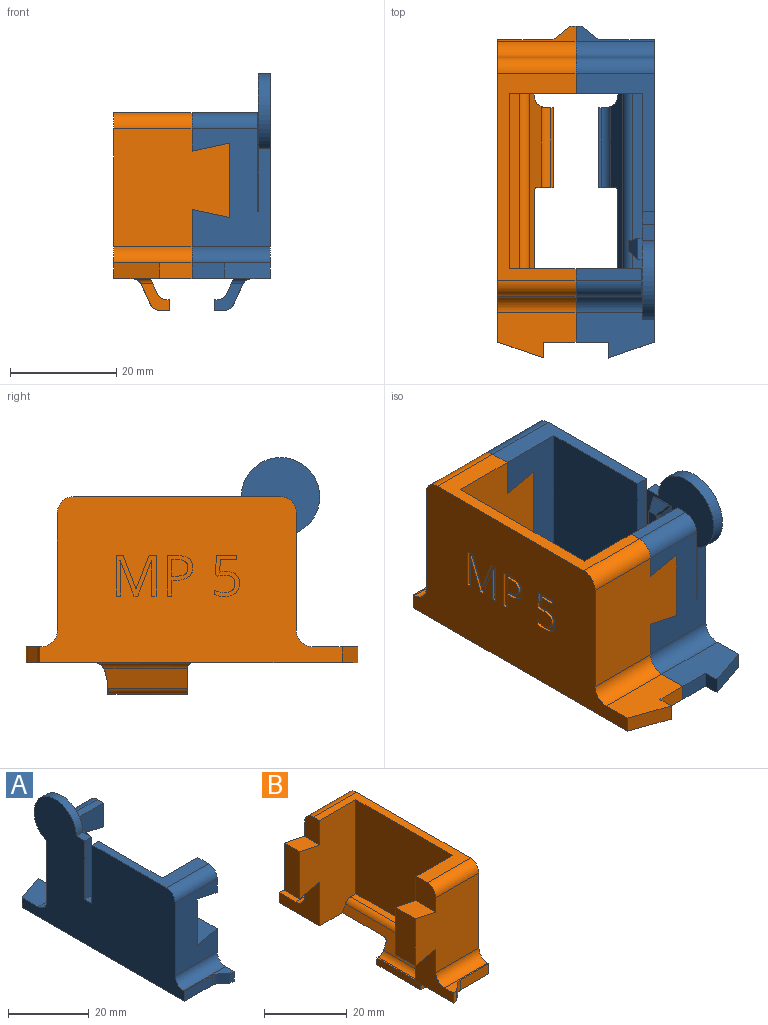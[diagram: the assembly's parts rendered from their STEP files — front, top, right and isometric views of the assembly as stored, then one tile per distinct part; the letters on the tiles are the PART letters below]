
ASSEMBLY  parts=2 mates=1
PART A: 65 faces, bbox 14.9x62.7x44.8 mm
  f0: plane 12.25x2.18mm, normal (0,0,1), area 26.6mm2, adj f1,f2,f4,f54
  f1: plane 31.2x12.45mm, normal (0,-1,0), area 284.9mm2, adj f0,f4,f8,f18,f28,f31,f34,f39
  f2: cylinder r=3mm len=12.25mm, axis (1,0,0), area 57.7mm2, adj f0,f4,f14,f54
  f3: plane 26.1x14.75mm, normal (0,0,1), area 107.6mm2, adj f6,f7,f17,f20,f31,f48
  f4: plane 7.2x5.18mm, normal (1,0,0), area 35.3mm2, adj f0,f1,f2,f14,f42
  f5: plane 22.2x14.75mm, normal (0,-1,0), area 239.9mm2, adj f7,f16,f17,f20,f38,f43,f44,f45
  f6: plane 31.2x12.45mm, normal (0,1,0), area 288.6mm2, adj f3,f7,f8,f18,f28,f31,f34,f38
  f7: plane 7.2x6.82mm, normal (1,0,0), area 47.2mm2, adj f3,f5,f6,f17,f43
  f8: plane 62.5x14.75mm, normal (0,0,-1), area 536.5mm2, adj f1,f6,f11,f12,f20,f21,f22,f23
  f9: plane 3x2.3mm, normal (0,0,1), area 6.9mm2, adj f20,f31,f46,f49
  f10: plane 14.75x8.6mm, normal (0,0,1), area 95.6mm2, adj f12,f15,f20,f23,f24,f39
  f11: cylinder r=4.2mm len=3mm, axis (0,0,-1), area 4.4mm2, adj f8,f13,f22,f38
  f12: plane 6.1x3mm, normal (0,1,0), area 18.3mm2, adj f8,f10,f23,f39
  f13: plane 14.75x2.9mm, normal (0,0,1), area 11.5mm2, adj f11,f16,f20,f21,f22,f37,f38
  f14: plane 22.2x14.75mm, normal (0,1,0), area 228.2mm2, adj f2,f4,f15,f20,f31,f39,f40,f41
  f15: cylinder r=3mm len=14.75mm, axis (1,0,0), area 69.5mm2, adj f10,f14,f20,f39
  f16: cylinder r=3mm len=14.75mm, axis (-1,0,0), area 69.5mm2, adj f5,f13,f20,f38
  f17: cylinder r=3mm len=14.75mm, axis (-1,0,0), area 69.5mm2, adj f3,f5,f7,f20
  f18: plane 33x1.8mm, normal (0,0,1), area 59.2mm2, adj f1,f6,f31,f34
  f19: plane 14.98x1.7mm, normal (0,0,-1), area 25.5mm2, adj f26,f29,f30,f36
  f20: plane 56.9x38.6mm, normal (-1,0,0), area 1504.8mm2, adj f3,f5,f8,f9,f10,f13,f14,f15
  f21: plane 9.74x3mm, normal (0,-1,0), area 29.2mm2, adj f8,f13,f20,f37
  f22: plane 3x2.32mm, normal (-0.63,-0.77,0), area 9mm2, adj f8,f11,f13,f37
  f23: plane 3x3mm, normal (1,0,0), area 9mm2, adj f8,f10,f12,f24
  f24: plane 8.65x3mm, normal (-0.33,0.94,0), area 27.5mm2, adj f8,f10,f20,f23
  f25: plane 15.86x3.81mm, normal (-0.91,0,-0.42), area 61.8mm2, adj f29,f30,f32,f36
  f26: plane 15.06x2.01mm, normal (1,0,0), area 30mm2, adj f19,f27,f29,f30
  f27: plane 15.04x0.42mm, normal (0,0,1), area 6.3mm2, adj f26,f29,f30,f35
  f28: plane 33.19x5.18mm, normal (0.91,0,0.42), area 127.4mm2, adj f1,f6,f8,f29,f30,f33,f34,f35
  f29: plane 5.3x5mm, normal (0,1,0), area 13.5mm2, adj f19,f25,f26,f27,f28,f32,f33,f35
  f30: extruded ~7.03x6mm, area 18.6mm2, adj f8,f19,f25,f26,f27,f28,f32,f35
  f31: plane 42.58x35.3mm, normal (1,0,0), area 1059.9mm2, adj f1,f3,f6,f9,f14,f18,f46,f47
  f32: cylinder r=2mm len=18.3mm, axis (0,-1,0), area 38.4mm2, adj f8,f25,f29,f30,f33
  f33: cylinder r=1mm len=3.94mm, axis (1,0,0), area 4.5mm2, adj f8,f28,f29,f32
  f34: cylinder r=2mm len=33mm, axis (0,1,0), area 75.1mm2, adj f1,f6,f18,f28
  f35: cylinder r=2mm len=15.24mm, axis (0,-1,0), area 34.4mm2, adj f27,f28,f29,f30
  f36: cylinder r=2mm len=14.98mm, axis (0,1,0), area 34.1mm2, adj f19,f25,f29,f30
  f37: cylinder r=2mm len=3mm, axis (0,0,-1), area 4.1mm2, adj f8,f13,f21,f22
  f38: plane 13x12.72mm, normal (1,0,0), area 108.4mm2, adj f5,f6,f8,f11,f13,f16,f44
  f39: plane 13.78x13mm, normal (1,0,0), area 95mm2, adj f1,f8,f10,f12,f14,f15,f41
  f40: plane 14x5.18mm, normal (1,0,0), area 72.5mm2, adj f1,f14,f41,f42
  f41: plane 7x5.18mm, normal (-0.21,0,0.98), area 37.1mm2, adj f1,f14,f39,f40
  f42: plane 7x5.18mm, normal (-0.21,0,-0.98), area 37.1mm2, adj f1,f4,f14,f40
  f43: plane 7x6.82mm, normal (-0.21,0,-0.98), area 48.9mm2, adj f5,f6,f7,f45
  f44: plane 7x6.82mm, normal (-0.21,0,0.98), area 48.9mm2, adj f5,f6,f38,f45
  f45: plane 14x6.82mm, normal (1,0,0), area 95.5mm2, adj f5,f6,f43,f44
  f46: plane 17.7x2.3mm, normal (0,-1,0), area 40.7mm2, adj f9,f20,f31,f47
  f47: plane 2.5x2.3mm, normal (0,0,1), area 5.8mm2, adj f20,f31,f46,f48
  f48: plane 17.7x2.3mm, normal (0,1,0), area 40.7mm2, adj f3,f20,f31,f47
  f49: cylinder r=7.4mm len=14.8mm, axis (-1,0,0), area 73.1mm2, adj f9,f14,f20,f31
  f50: plane 5.01x1.5mm, normal (0.32,-0.95,0), area 6.3mm2, adj f31,f51,f57,f59
  f51: plane 4x1.5mm, normal (-0.01,0,-1), area 4.5mm2, adj f31,f50,f52,f60
  f52: plane 5.01x1.5mm, normal (0.71,0.71,0), area 8.5mm2, adj f31,f51,f55,f61
  f53: plane 5.18x0.2mm, normal (0,0,1), area 1mm2, adj f1,f14,f31,f54
  f54: plane 18.55x5.18mm, normal (-1,0,0), area 94mm2, adj f0,f1,f2,f14,f53
  f55: plane 2.61x2.5mm, normal (0.31,0.86,-0.41), area 3.1mm2, adj f52,f56,f62,f64
  f56: plane 4x0.8mm, normal (-0.6,0,0.8), area 4mm2, adj f31,f55,f57,f64
  f57: plane 2.61x2.5mm, normal (0.12,-0.98,-0.16), area 2.7mm2, adj f50,f56,f58,f64
  f58: plane 1x0.33mm, normal (-0.31,0,0.95), area 0mm2, adj f57,f59,f63
  f59: plane 3.33x1mm, normal (0,-1,0), area 3.2mm2, adj f50,f58,f60,f63
  f60: plane 2x1mm, normal (0,0,-1), area 2mm2, adj f51,f59,f61,f63
  f61: plane 3.33x1mm, normal (0,1,0), area 3.2mm2, adj f52,f60,f62,f63
  f62: plane 1x0.33mm, normal (-0.31,0,0.95), area 0.1mm2, adj f55,f61,f63
  f63: plane 3.33x2mm, normal (1,0,0), area 6.7mm2, adj f58,f59,f60,f61,f62,f64
  f64: plane 4x2.28mm, normal (0.8,0,0.6), area 8.1mm2, adj f55,f56,f57,f63
PART B: 100 faces, bbox 21.9x62.7x37.4 mm
  f0: plane 56.9x31.2mm, normal (1,0,0), area 1378.8mm2, adj f3,f4,f5,f8,f9,f12,f13,f14
  f1: plane 13.78x13mm, normal (-1,0,0), area 95mm2, adj f3,f5,f11,f13,f22,f26,f43
  f2: plane 7.2x6.82mm, normal (-1,0,0), area 47.2mm2, adj f4,f14,f21,f29,f38
  f3: plane 62.5x14.75mm, normal (0,0,-1), area 536.5mm2, adj f0,f1,f6,f7,f8,f9,f10,f11
  f4: plane 39x14.75mm, normal (0,0,1), area 164.4mm2, adj f0,f2,f21,f22,f24,f28,f29,f37
  f5: plane 14.75x8.6mm, normal (0,0,1), area 95.6mm2, adj f0,f1,f9,f10,f11,f26
  f6: cylinder r=4.2mm len=3mm, axis (0,0,-1), area 4.4mm2, adj f3,f7,f12,f36
  f7: plane 3x2.32mm, normal (0.63,-0.77,0), area 9mm2, adj f3,f6,f12,f35
  f8: plane 9.74x3mm, normal (0,-1,0), area 29.2mm2, adj f0,f3,f12,f35
  f9: plane 8.65x3mm, normal (0.33,0.94,0), area 27.5mm2, adj f0,f3,f5,f10
  f10: plane 3x3mm, normal (-1,0,0), area 9mm2, adj f3,f5,f9,f11
  f11: plane 6.1x3mm, normal (0,1,0), area 18.3mm2, adj f1,f3,f5,f10
  f12: plane 14.75x2.9mm, normal (0,0,1), area 11.5mm2, adj f0,f6,f7,f8,f27,f35,f36
  f13: plane 22.2x21.75mm, normal (0,1,0), area 415mm2, adj f0,f1,f26,f28,f37,f41,f42,f43
  f14: plane 22.2x21.75mm, normal (0,-1,0), area 415mm2, adj f0,f2,f27,f29,f36,f38,f39,f40
  f15: plane 15.06x2.01mm, normal (-1,0,0), area 30mm2, adj f16,f19,f20,f23
  f16: plane 14.98x1.7mm, normal (0,0,-1), area 25.5mm2, adj f15,f20,f23,f34
  f17: plane 15.86x3.81mm, normal (0.91,0,-0.42), area 61.8mm2, adj f20,f23,f30,f34
  f18: plane 33.19x5.18mm, normal (-0.91,0,0.42), area 127.4mm2, adj f3,f20,f21,f22,f23,f31,f32,f33
  f19: plane 15.04x0.42mm, normal (0,0,1), area 6.3mm2, adj f15,f20,f23,f33
  f20: plane 5.3x5mm, normal (0,1,0), area 13.5mm2, adj f15,f16,f17,f18,f19,f30,f31,f33
  f21: plane 31.2x19.45mm, normal (0,1,0), area 463.6mm2, adj f2,f3,f4,f18,f24,f25,f32,f36
  f22: plane 31.2x19.45mm, normal (0,-1,0), area 463.6mm2, adj f1,f3,f4,f18,f24,f25,f32,f37
  f23: extruded ~7.03x6mm, area 18.6mm2, adj f3,f15,f16,f17,f18,f19,f30,f33
  f24: plane 33x27.9mm, normal (-1,0,0), area 920.7mm2, adj f4,f21,f22,f25
  f25: plane 33x1.8mm, normal (0,0,1), area 59.2mm2, adj f21,f22,f24,f32
  f26: cylinder r=3mm len=14.75mm, axis (1,0,0), area 69.5mm2, adj f0,f1,f5,f13
  f27: cylinder r=3mm len=14.75mm, axis (-1,0,0), area 69.5mm2, adj f0,f12,f14,f36
  f28: cylinder r=3mm len=14.75mm, axis (1,0,0), area 69.5mm2, adj f0,f4,f13,f37
  f29: cylinder r=3mm len=14.75mm, axis (-1,0,0), area 69.5mm2, adj f0,f2,f4,f14
  f30: cylinder r=2mm len=18.3mm, axis (0,1,0), area 38.4mm2, adj f3,f17,f20,f23,f31
  f31: cylinder r=1mm len=3.94mm, axis (-1,0,0), area 4.5mm2, adj f3,f18,f20,f30
  f32: cylinder r=2mm len=33mm, axis (0,-1,0), area 75.1mm2, adj f18,f21,f22,f25
  f33: cylinder r=2mm len=15.24mm, axis (0,-1,0), area 34.4mm2, adj f18,f19,f20,f23
  f34: cylinder r=2mm len=14.98mm, axis (0,1,0), area 34.1mm2, adj f16,f17,f20,f23
  f35: cylinder r=2mm len=3mm, axis (0,0,1), area 4.1mm2, adj f3,f7,f8,f12
  f36: plane 13x12.72mm, normal (-1,0,0), area 108.4mm2, adj f3,f6,f12,f14,f21,f27,f39
  f37: plane 7.2x5.18mm, normal (-1,0,0), area 35.3mm2, adj f4,f13,f22,f28,f41
  f38: plane 7x6.82mm, normal (0.21,0,0.98), area 48.9mm2, adj f2,f14,f21,f40
  f39: plane 7x6.82mm, normal (0.21,0,-0.98), area 48.9mm2, adj f14,f21,f36,f40
  f40: plane 14x6.82mm, normal (-1,0,0), area 95.5mm2, adj f14,f21,f38,f39
  f41: plane 7x5.18mm, normal (0.21,0,0.98), area 37.1mm2, adj f13,f22,f37,f42
  f42: plane 14x5.18mm, normal (-1,0,0), area 72.5mm2, adj f13,f22,f41,f43
  f43: plane 7x5.18mm, normal (0.21,0,-0.98), area 37.1mm2, adj f1,f13,f22,f42
  f44: plane 0.8x0.5mm, normal (0,0,-1), area 0.4mm2, adj f45,f58,f59,f99
  f45: plane 3.09x0.5mm, normal (0,-1,0), area 1.5mm2, adj f44,f46,f59,f99
  f46: plane 0.99x0.5mm, normal (0,0,1), area 0.5mm2, adj f45,f47,f59,f99
  f47: extruded ~1.54x0.5mm, area 0.8mm2, adj f46,f48,f59,f99
  f48: extruded ~1.12x0.5mm, area 0.6mm2, adj f47,f49,f59,f99
  f49: extruded ~1.22x0.53mm, area 0.7mm2, adj f48,f58,f59,f99
  f50: extruded ~1.78x0.79mm, area 1mm2, adj f0,f51,f57,f59
  f51: extruded ~2.85x2.22mm, area 2.1mm2, adj f0,f50,f52,f59
  f52: plane 1.98x0.5mm, normal (0,0,-1), area 1mm2, adj f0,f51,f53,f59
  f53: plane 7.62x0.5mm, normal (0,1,0), area 3.8mm2, adj f0,f52,f54,f59
  f54: plane 0.89x0.5mm, normal (0,0,1), area 0.4mm2, adj f0,f53,f55,f59
  f55: plane 3x0.5mm, normal (0,-1,0), area 1.5mm2, adj f0,f54,f56,f59
  f56: plane 0.9x0.5mm, normal (0,0,1), area 0.4mm2, adj f0,f55,f57,f59
  f57: extruded ~2.26x0.62mm, area 1.2mm2, adj f0,f50,f56,f59
  f58: extruded ~1.7x0.5mm, area 0.9mm2, adj f44,f49,f59,f99
  f59: plane 7.62x4.83mm, normal (1,0,0), area 14.3mm2, adj f44,f45,f46,f47,f48,f49,f50,f51
  f60: extruded ~1.89x0.6mm, area 1mm2, adj f0,f61,f78,f79
  f61: extruded ~1.19x0.5mm, area 0.6mm2, adj f0,f60,f62,f79
  f62: plane 2.29x0.5mm, normal (0,-1,0.08), area 1.1mm2, adj f0,f61,f63,f79
  f63: plane 3.05x0.5mm, normal (0,0,1), area 1.5mm2, adj f0,f62,f64,f79
  f64: plane 0.8x0.5mm, normal (0,-1,0), area 0.4mm2, adj f0,f63,f65,f79
  f65: plane 3.79x0.5mm, normal (0,0,-1), area 1.9mm2, adj f0,f64,f66,f79
  f66: plane 3.56x0.5mm, normal (0,1,-0.08), area 1.8mm2, adj f0,f65,f67,f79
  f67: plane 0.5x0.45mm, normal (0,0.54,0.84), area 0.3mm2, adj f0,f66,f68,f79
  f68: extruded ~1.32x0.5mm, area 0.7mm2, adj f0,f67,f69,f79
  f69: extruded ~1.95x1.59mm, area 1.4mm2, adj f0,f68,f70,f79
  f70: extruded ~1.25x0.51mm, area 0.7mm2, adj f0,f69,f71,f79
  f71: extruded ~1.42x0.5mm, area 0.8mm2, adj f0,f70,f72,f79
  f72: extruded ~1.07x0.5mm, area 0.5mm2, adj f0,f71,f73,f79
  f73: extruded ~0.91x0.5mm, area 0.5mm2, adj f0,f72,f74,f79
  f74: plane 0.83x0.5mm, normal (0,1,0), area 0.4mm2, adj f0,f73,f75,f79
  f75: extruded ~1.96x0.5mm, area 1mm2, adj f0,f74,f76,f79
  f76: extruded ~2.08x0.67mm, area 1.1mm2, adj f0,f75,f77,f79
  f77: extruded ~1.85x0.75mm, area 1mm2, adj f0,f76,f78,f79
  f78: extruded ~1.63x0.69mm, area 0.9mm2, adj f0,f60,f77,f79
  f79: plane 7.72x4.79mm, normal (1,0,0), area 13.5mm2, adj f60,f61,f62,f63,f64,f65,f66,f67
  f80: plane 6.75x2.58mm, normal (0,0.93,0.36), area 3.6mm2, adj f0,f81,f97,f98
  f81: plane 0.71x0.5mm, normal (0,0,1), area 0.4mm2, adj f0,f80,f82,f98
  f82: plane 6.74x2.61mm, normal (0,-0.93,0.36), area 3.6mm2, adj f0,f81,f83,f98
  f83: plane 0.5x0.04mm, normal (0,0,1), area 0mm2, adj f0,f82,f84,f98
  f84: extruded ~1.83x0.5mm, area 0.9mm2, adj f0,f83,f85,f98
  f85: plane 4.91x0.5mm, normal (0,1,0), area 2.5mm2, adj f0,f84,f86,f98
  f86: plane 0.89x0.5mm, normal (0,0,1), area 0.4mm2, adj f0,f85,f87,f98
  f87: plane 7.62x0.5mm, normal (0,-1,0), area 3.8mm2, adj f0,f86,f88,f98
  f88: plane 1.32x0.5mm, normal (0,0,-1), area 0.7mm2, adj f0,f87,f89,f98
  f89: plane 6.28x2.43mm, normal (0,0.93,-0.36), area 3.4mm2, adj f0,f88,f90,f98
  f90: plane 0.5x0.04mm, normal (0,0,-1), area 0mm2, adj f0,f89,f91,f98
  f91: plane 6.28x2.41mm, normal (0,-0.93,-0.36), area 3.4mm2, adj f0,f90,f92,f98
  f92: plane 1.33x0.5mm, normal (0,0,-1), area 0.7mm2, adj f0,f91,f93,f98
  f93: plane 7.62x0.5mm, normal (0,1,0), area 3.8mm2, adj f0,f92,f94,f98
  f94: plane 0.82x0.5mm, normal (0,0,1), area 0.4mm2, adj f0,f93,f95,f98
  f95: plane 4.84x0.5mm, normal (0,-1,0), area 2.4mm2, adj f0,f94,f96,f98
  f96: extruded ~1.91x0.5mm, area 1mm2, adj f0,f95,f97,f98
  f97: plane 0.5x0.04mm, normal (0,0,1), area 0mm2, adj f0,f80,f96,f98
  f98: plane 7.62x7.54mm, normal (1,0,0), area 24.8mm2, adj f80,f81,f82,f83,f84,f85,f86,f87
  f99: plane 3.09x3.03mm, normal (1,0,0), area 8.3mm2, adj f44,f45,f46,f47,f48,f49,f58
PLACE A rot(axis=(0,0,1),180deg) t=(25.75,-3.62,3.19)mm
PLACE B rot(axis=(0,0,1),180deg) t=(25.75,-3.62,3.19)mm fixed
MATE parallel B.f13 <-> A.f14  axis (0,-1,0) through (32.75,-26.12,21.69)mm
